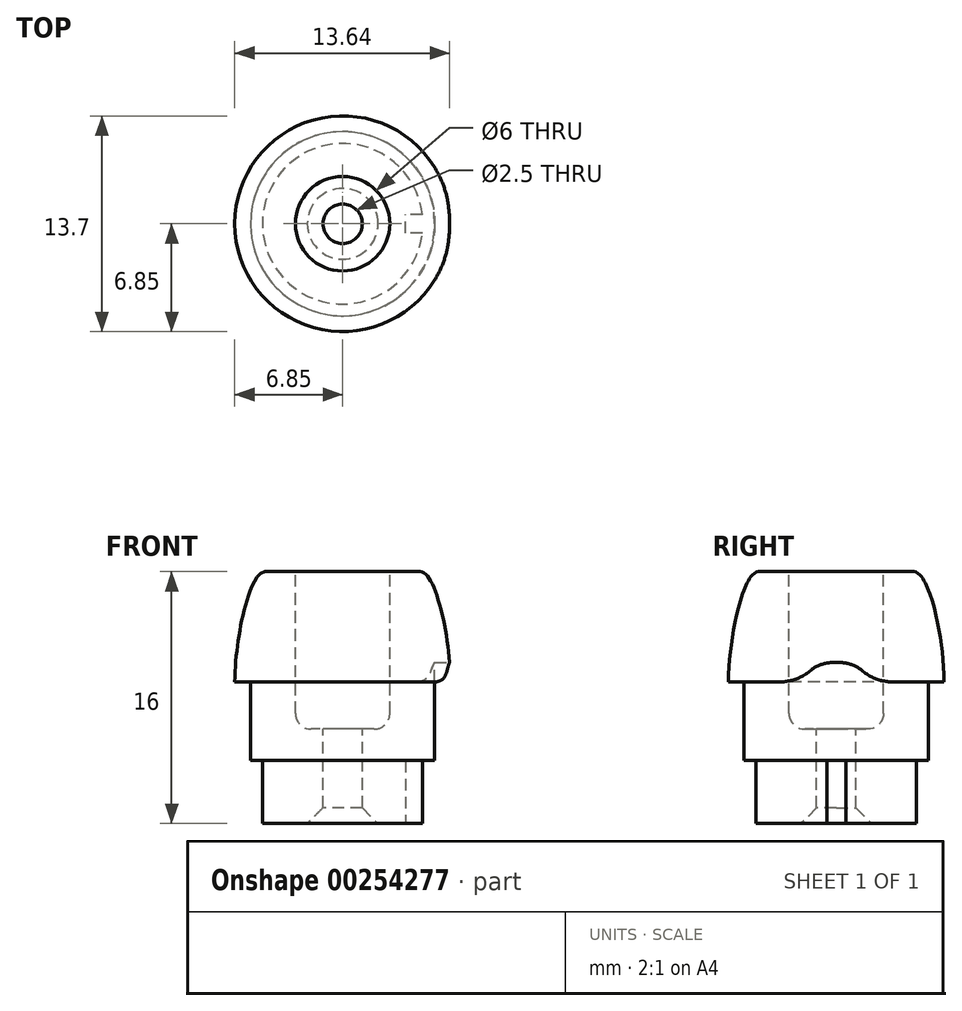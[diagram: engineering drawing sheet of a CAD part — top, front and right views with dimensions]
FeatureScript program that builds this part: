
annotation { "Feature Type Name" : "Feature", "Feature Type Description" : "" }
export const myFeature = defineFeature(function(context is Context, id is Id, definition is map)
    precondition{}
    {
        {
            var Q0;
            Q0=qCreatedBy(makeId("Front.planeOp"),FACE);
            var sketch = newSketch(context, id + "F0", { "sketchPlane" : qUnion([Q0])});
            skLineSegment(sketch, "E0", {"start": v(0, 16) * mm, "end": v(0, 0) * mm, "construction": true});
            skLineSegment(sketch, "E1", {"start": v(1.25, 0) * mm, "end": v(1.25, 6) * mm});
            skLineSegment(sketch, "E2", {"start": v(1.25, 6) * mm, "end": v(3, 6) * mm});
            skLineSegment(sketch, "E3", {"start": v(3, 6) * mm, "end": v(3, 16) * mm});
            skLineSegment(sketch, "E4", {"start": v(3, 16) * mm, "end": v(6.85, 16) * mm, "construction": true});
            skLineSegment(sketch, "E5", {"start": v(6.85, 16) * mm, "end": v(6.85, 9) * mm, "construction": true});
            skLineSegment(sketch, "E6", {"start": v(6.85, 9) * mm, "end": v(5.85, 9) * mm});
            skLineSegment(sketch, "E7", {"start": v(5.85, 9) * mm, "end": v(5.85, 4) * mm});
            skLineSegment(sketch, "E8", {"start": v(5.85, 4) * mm, "end": v(5.1, 4) * mm});
            skLineSegment(sketch, "E9", {"start": v(5.1, 4) * mm, "end": v(5.1, 0) * mm});
            skLineSegment(sketch, "E10", {"start": v(5.1, 0) * mm, "end": v(1.25, 0) * mm});
            skFitSpline(sketch, "E11", {"points": [v(6.85, 9) * mm, v(4.92, 16) * mm], "startDerivative": vector(0, 7.6) * mm, "endDerivative": vector(-3.15, 0) * mm});
            skPoint(sketch, "E12", {"position": v(6.85, 12.5) * mm});
            skLineSegment(sketch, "E13", {"start": v(3, 16) * mm, "end": v(4.92, 16) * mm});
            skSolve(sketch);
        }
        {
            var Q0;
            Q0=makeQuery(id+"F0.imprint","IMPRINT",FACE,{"disambiguationData":[TD([[makeQuery(id+"F0.imprint","IMPRINT",EDGE,{"derivedFrom":sQuery(id+"F0.wireOp",EDGE,"E1")}),-1.0]])]});
            var Q1;
            Q1=sQuery(id+"F0.wireOp",EDGE,"E0");
            revolve(context, id + "F1", {"surfaceOperationType" : NewSurfaceOperationType.NEW, "entities" : qUnion([Q0]), "axis" : qUnion([Q1]), "revolveType" : RevolveType.FULL});
        }
        {
            var Q0;
            Q0=makeQuery(id+"F1.opRevolve","SWEPT_EDGE",EDGE,{"disambiguationData":[OSD([sQuery(id+"F0.wireOp",EDGE,"E1"),sQuery(id+"F0.wireOp",EDGE,"E10")])]});
            chamfer(context, id + "F2", {"entities" : qUnion([Q0]), "width" : 1 * mm, "tangentPropagation" : true});
        }
        {
            var Q0;
            Q0=sQuery(id+"F0.wireOp",VERTEX,"E5.end");
            var Q1;
            Q1=sQuery(id+"F0.wireOp",EDGE,"E6");
            cPlane(context, id + "F3", {"entities" : qUnion([Q0, Q1]), "cplaneType" : CPlaneType.LINE_POINT, "offset" : 25 * mm, "width" : 150 * mm, "height" : 150 * mm});
        }
        {
            var Q0;
            Q0=qCreatedBy(id+"F3.planeOp",FACE);
            var sketch = newSketch(context, id + "F4", { "sketchPlane" : qUnion([Q0])});
            skPoint(sketch, "E14.0", {"position": v(0, 9) * mm});
            skEllipse(sketch, "E15", {"center": v(0, 9) * mm, "majorRadius": 2 * mm, "minorRadius": 1.25 * mm, "majorAxis": v(1, 0)});
            skPoint(sketch, "E16", {"position": v(-2, 9) * mm});
            skSolve(sketch);
        }
        {
            var Q0;
            Q0=makeQuery(id+"F4.imprint","IMPRINT",FACE,{"disambiguationData":[TD([[makeQuery(id+"F4.imprint","IMPRINT",EDGE,{"derivedFrom":sQuery(id+"F4.wireOp",EDGE,"E15")}),1.0]])]});
            var Q1;
            Q1=makeQuery(id+"F1.opRevolve","SWEPT_FACE",FACE,{"disambiguationData":[OSD([sQuery(id+"F0.wireOp",EDGE,"E7")])]});
            extrude(context, id + "F5", {"entities" : qUnion([Q0]), "operationType" : NewBodyOperationType.REMOVE, "endBound" : BoundingType.UP_TO_SURFACE, "depth" : 25 * mm, "endBoundEntityFace" : qUnion([Q1]), "offsetDistance" : 25 * mm});
        }
        {
            var Q0;
            Q0=makeQuery(id+"F1.opRevolve","SWEPT_FACE",FACE,{"disambiguationData":[OSD([sQuery(id+"F0.wireOp",EDGE,"E10")])]});
            var sketch = newSketch(context, id + "F6", { "sketchPlane" : qUnion([Q0])});
            skPoint(sketch, "E17.0", {"position": v(5.1, 0) * mm});
            skLineSegment(sketch, "E18.bottom", {"start": v(5.1, 0.6) * mm, "end": v(4, 0.6) * mm});
            skLineSegment(sketch, "E18.top", {"start": v(5.1, -0.6) * mm, "end": v(4, -0.6) * mm});
            skLineSegment(sketch, "E18.left", {"start": v(5.1, 0.6) * mm, "end": v(5.1, -0.6) * mm});
            skLineSegment(sketch, "E18.right", {"start": v(4, 0.6) * mm, "end": v(4, -0.6) * mm});
            skSolve(sketch);
        }
        {
            var Q0;
            {var subQ4=sQuery(id+"F6.wireOp",EDGE,"E18.right");Q0=makeQuery(id+"F6.imprint","IMPRINT",FACE,{"disambiguationData":[TD([[makeQuery(id+"F6.imprint","IMPRINT",EDGE,{"derivedFrom":subQ4}),1.0]])]});}
            var Q1;
            Q1=makeQuery(id+"F1.opRevolve","SWEPT_FACE",FACE,{"disambiguationData":[OSD([sQuery(id+"F0.wireOp",EDGE,"E8")])]});
            extrude(context, id + "F7", {"entities" : qUnion([Q0]), "operationType" : NewBodyOperationType.REMOVE, "endBound" : BoundingType.UP_TO_SURFACE, "oppositeDirection" : true, "depth" : 25 * mm, "endBoundEntityFace" : qUnion([Q1]), "offsetDistance" : 25 * mm});
        }
        {
            var Q0;
            Q0=makeQuery(id+"F5.boolean.opBoolean","INTERSECT",EDGE,{"disambiguationData":[OD(0.0)],"derivedFrom":[makeQuery(id+"F1.opRevolve","SWEPT_FACE",FACE,{"disambiguationData":[OSD([sQuery(id+"F0.wireOp",EDGE,"E6")])]}),makeQuery(id+"F5.opExtrude","SWEPT_FACE",FACE,{"disambiguationData":[OSD([sQuery(id+"F4.wireOp",EDGE,"E15")])]})]});
            var Q1;
            Q1=makeQuery(id+"F5.boolean.opBoolean","INTERSECT",EDGE,{"disambiguationData":[OD(1.0)],"derivedFrom":[makeQuery(id+"F1.opRevolve","SWEPT_FACE",FACE,{"disambiguationData":[OSD([sQuery(id+"F0.wireOp",EDGE,"E6")])]}),makeQuery(id+"F5.opExtrude","SWEPT_FACE",FACE,{"disambiguationData":[OSD([sQuery(id+"F4.wireOp",EDGE,"E15")])]})]});
            fillet(context, id + "F8", {"entities" : qUnion([Q0, Q1]), "tangentPropagation" : true, "radius" : 3 * mm, "defaultsChanged" : true, "vertexSettings" : [], "allowEdgeOverflow" : false});
        }
        {
            var Q0;
            Q0=makeQuery(id+"F1.opRevolve","SWEPT_EDGE",EDGE,{"disambiguationData":[OSD([sQuery(id+"F0.wireOp",EDGE,"E2"),sQuery(id+"F0.wireOp",EDGE,"E3")])]});
            fillet(context, id + "F9", {"entities" : qUnion([Q0]), "tangentPropagation" : true, "radius" : 1 * mm, "defaultsChanged" : true, "vertexSettings" : [], "allowEdgeOverflow" : false});
        }
    });
